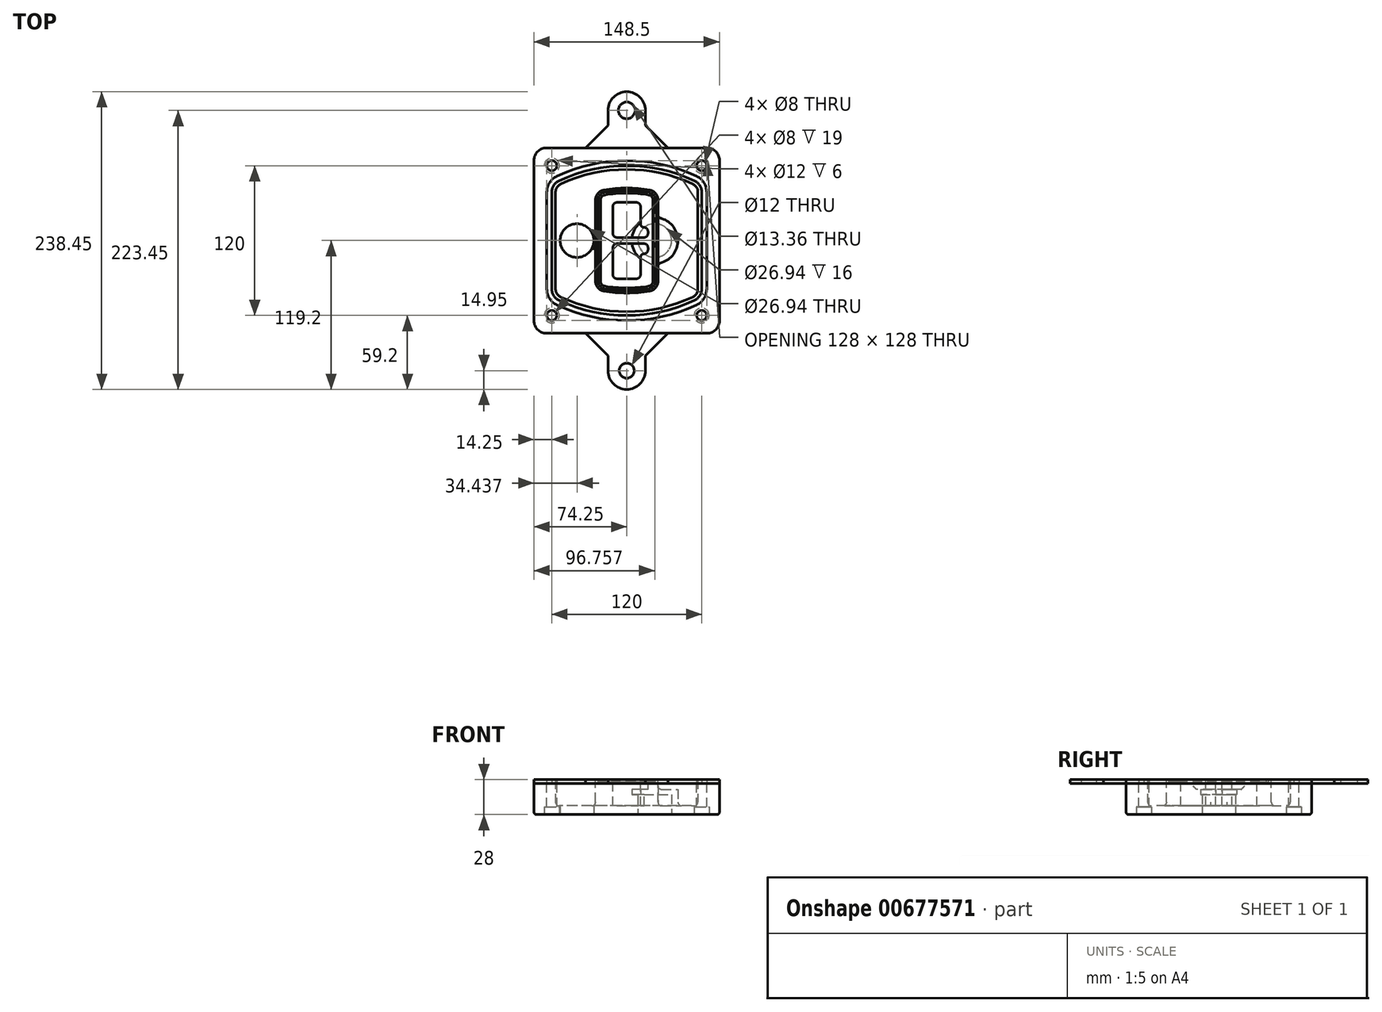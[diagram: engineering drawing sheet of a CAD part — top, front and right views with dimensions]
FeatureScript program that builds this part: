
annotation { "Feature Type Name" : "Feature", "Feature Type Description" : "" }
export const myFeature = defineFeature(function(context is Context, id is Id, definition is map)
    precondition{}
    {
        {
            var Q0;
            Q0=qCreatedBy(makeId("Top.planeOp"),FACE);
            var sketch = newSketch(context, id + "F0", { "sketchPlane" : qUnion([Q0])});
            skPoint(sketch, "E0.rect.middle", {"position": v(0, 0) * mm});
            skLineSegment(sketch, "E1.bottom", {"start": v(-64.25, -74.25) * mm, "end": v(64.25, -74.25) * mm});
            skLineSegment(sketch, "E1.top", {"start": v(-64.25, 74.25) * mm, "end": v(64.25, 74.25) * mm});
            skLineSegment(sketch, "E1.left", {"start": v(-74.25, -64.25) * mm, "end": v(-74.25, 64.25) * mm});
            skLineSegment(sketch, "E1.right", {"start": v(74.25, -64.25) * mm, "end": v(74.25, 64.25) * mm});
            skLineSegment(sketch, "E2", {"start": v(-74.25, 74.25) * mm, "end": v(74.25, -74.25) * mm, "construction": true});
            skLineSegment(sketch, "E3", {"start": v(74.25, 74.25) * mm, "end": v(-74.25, -74.25) * mm, "construction": true});
            skCircle(sketch, "E4", {"center": v(-60, 60) * mm, "radius": 4 * mm});
            skCircle(sketch, "E5", {"center": v(60, 60) * mm, "radius": 4 * mm});
            skCircle(sketch, "E6", {"center": v(60, -60) * mm, "radius": 4 * mm});
            skCircle(sketch, "E7", {"center": v(-60, -60) * mm, "radius": 4 * mm});
            skLineSegment(sketch, "E8", {"start": v(-60, 60) * mm, "end": v(60, 60) * mm, "construction": true});
            skLineSegment(sketch, "E9", {"start": v(60, 60) * mm, "end": v(60, -60) * mm, "construction": true});
            skLineSegment(sketch, "E10", {"start": v(60, -60) * mm, "end": v(-60, -60) * mm, "construction": true});
            skLineSegment(sketch, "E11", {"start": v(-60, -60) * mm, "end": v(-60, 60) * mm, "construction": true});
            skLineSegment(sketch, "E12", {"start": v(-60, 38.83) * mm, "end": v(-60, -38.83) * mm});
            skLineSegment(sketch, "E13", {"start": v(60, 38.83) * mm, "end": v(60, -38.83) * mm});
            skArc(sketch, "E14", {"start": v(54.26, 47.88) * mm, "mid": v(0, 60) * mm, "end": v(-54.26, 47.88) * mm});
            skArc(sketch, "E15", {"start": v(-54.26, -47.88) * mm, "mid": v(0, -60) * mm, "end": v(54.26, -47.88) * mm});
            skLineSegment(sketch, "E16", {"start": v(-60, 0) * mm, "end": v(60, 0) * mm, "construction": true});
            skPoint(sketch, "E17.visualSharp", {"position": v(-60, -45) * mm});
            skArc(sketch, "E17.filletArc", {"start": v(-60, -38.83) * mm, "mid": v(-58.44, -44.2) * mm, "end": v(-54.26, -47.88) * mm});
            skPoint(sketch, "E18.visualSharp", {"position": v(-60, 45) * mm});
            skArc(sketch, "E18.filletArc", {"start": v(-54.26, 47.88) * mm, "mid": v(-58.44, 44.2) * mm, "end": v(-60, 38.83) * mm});
            skPoint(sketch, "E19.visualSharp", {"position": v(60, 45) * mm});
            skArc(sketch, "E19.filletArc", {"start": v(60, 38.83) * mm, "mid": v(58.44, 44.2) * mm, "end": v(54.26, 47.88) * mm});
            skPoint(sketch, "E20.visualSharp", {"position": v(60, -45) * mm});
            skArc(sketch, "E20.filletArc", {"start": v(54.26, -47.88) * mm, "mid": v(58.44, -44.2) * mm, "end": v(60, -38.83) * mm});
            skPoint(sketch, "E21.visualSharp", {"position": v(-74.25, 74.25) * mm});
            skArc(sketch, "E21.filletArc", {"start": v(-64.25, 74.25) * mm, "mid": v(-71.32, 71.32) * mm, "end": v(-74.25, 64.25) * mm});
            skPoint(sketch, "E22.visualSharp", {"position": v(74.25, 74.25) * mm});
            skArc(sketch, "E22.filletArc", {"start": v(74.25, 64.25) * mm, "mid": v(71.32, 71.32) * mm, "end": v(64.25, 74.25) * mm});
            skPoint(sketch, "E23.visualSharp", {"position": v(74.25, -74.25) * mm});
            skArc(sketch, "E23.filletArc", {"start": v(64.25, -74.25) * mm, "mid": v(71.32, -71.32) * mm, "end": v(74.25, -64.25) * mm});
            skPoint(sketch, "E24.visualSharp", {"position": v(-74.25, -74.25) * mm});
            skArc(sketch, "E24.filletArc", {"start": v(-74.25, -64.25) * mm, "mid": v(-71.32, -71.32) * mm, "end": v(-64.25, -74.25) * mm});
            skArc(sketch, "E25.0", {"start": v(57, 38.83) * mm, "mid": v(55.9, 42.58) * mm, "end": v(52.98, 45.17) * mm});
            skLineSegment(sketch, "E25.1", {"start": v(57, 38.83) * mm, "end": v(57, -38.83) * mm});
            skArc(sketch, "E25.2", {"start": v(52.98, -45.17) * mm, "mid": v(55.9, -42.58) * mm, "end": v(57, -38.83) * mm});
            skArc(sketch, "E25.3", {"start": v(-52.98, -45.17) * mm, "mid": v(0, -57) * mm, "end": v(52.98, -45.17) * mm});
            skArc(sketch, "E25.4", {"start": v(-57, -38.83) * mm, "mid": v(-55.9, -42.58) * mm, "end": v(-52.98, -45.17) * mm});
            skArc(sketch, "E25.5", {"start": v(52.98, 45.17) * mm, "mid": v(0, 57) * mm, "end": v(-52.98, 45.17) * mm});
            skLineSegment(sketch, "E25.6", {"start": v(-57, 38.83) * mm, "end": v(-57, -38.83) * mm});
            skArc(sketch, "E25.7", {"start": v(-52.98, 45.17) * mm, "mid": v(-55.9, 42.58) * mm, "end": v(-57, 38.83) * mm});
            skArc(sketch, "E26.0", {"start": v(-55.96, 51.5) * mm, "mid": v(-61.82, 46.33) * mm, "end": v(-64, 38.83) * mm});
            skArc(sketch, "E26.1", {"start": v(55.96, 51.5) * mm, "mid": v(0, 64) * mm, "end": v(-55.96, 51.5) * mm});
            skArc(sketch, "E26.2", {"start": v(64, 38.83) * mm, "mid": v(61.82, 46.33) * mm, "end": v(55.96, 51.5) * mm});
            skLineSegment(sketch, "E26.3", {"start": v(64, 38.83) * mm, "end": v(64, -38.83) * mm});
            skArc(sketch, "E26.4", {"start": v(55.96, -51.5) * mm, "mid": v(61.82, -46.33) * mm, "end": v(64, -38.83) * mm});
            skLineSegment(sketch, "E26.5", {"start": v(-64, 38.83) * mm, "end": v(-64, -38.83) * mm});
            skArc(sketch, "E26.6", {"start": v(-55.96, -51.5) * mm, "mid": v(0, -64) * mm, "end": v(55.96, -51.5) * mm});
            skArc(sketch, "E26.7", {"start": v(-64, -38.83) * mm, "mid": v(-61.82, -46.33) * mm, "end": v(-55.96, -51.5) * mm});
            skSolve(sketch);
        }
        {
            var Q0;
            Q0=makeQuery(id+"F0.imprint","IMPRINT",FACE,{"disambiguationData":[TD([[makeQuery(id+"F0.imprint","IMPRINT",EDGE,{"derivedFrom":sQuery(id+"F0.wireOp",EDGE,"E1.bottom")}),1.0]])]});
            var Q1;
            Q1=makeQuery(id+"F0.imprint","IMPRINT",FACE,{"disambiguationData":[TD([[makeQuery(id+"F0.imprint","IMPRINT",EDGE,{"derivedFrom":sQuery(id+"F0.wireOp",EDGE,"E12")}),1.0]])]});
            var Q2;
            Q2=makeQuery(id+"F0.imprint","IMPRINT",FACE,{"disambiguationData":[TD([[makeQuery(id+"F0.imprint","IMPRINT",EDGE,{"derivedFrom":sQuery(id+"F0.wireOp",EDGE,"E25.0")}),1.0]])]});
            var Q3;
            Q3=makeQuery(id+"F0.imprint","IMPRINT",FACE,{"disambiguationData":[TD([[makeQuery(id+"F0.imprint","IMPRINT",EDGE,{"derivedFrom":sQuery(id+"F0.wireOp",EDGE,"E12")}),-1.0]])]});
            extrude(context, id + "F1", {"entities" : qUnion([Q0, Q1, Q2, Q3]), "oppositeDirection" : true, "depth" : 25 * mm});
        }
        {
            var Q0;
            Q0=makeQuery(id+"F0.imprint","IMPRINT",FACE,{"disambiguationData":[TD([[makeQuery(id+"F0.imprint","IMPRINT",EDGE,{"derivedFrom":sQuery(id+"F0.wireOp",EDGE,"E12")}),1.0]])]});
            extrude(context, id + "F2", {"entities" : qUnion([Q0]), "operationType" : NewBodyOperationType.ADD, "depth" : 3 * mm});
        }
        {
            var Q0;
            Q0=makeQuery(id+"F0.imprint","IMPRINT",FACE,{"disambiguationData":[TD([[makeQuery(id+"F0.imprint","IMPRINT",EDGE,{"derivedFrom":sQuery(id+"F0.wireOp",EDGE,"E25.0")}),1.0]])]});
            extrude(context, id + "F3", {"entities" : qUnion([Q0]), "operationType" : NewBodyOperationType.REMOVE, "oppositeDirection" : true, "depth" : 18 * mm});
        }
        {
            var Q0;
            Q0=makeQuery(id+"F2.opExtrude","CAP_FACE",FACE,{"disambiguationData":[OSD([sQuery(id+"F0.wireOp",EDGE,"E12"),sQuery(id+"F0.wireOp",EDGE,"E13"),sQuery(id+"F0.wireOp",EDGE,"E14"),sQuery(id+"F0.wireOp",EDGE,"E15"),sQuery(id+"F0.wireOp",EDGE,"E17.filletArc"),sQuery(id+"F0.wireOp",EDGE,"E18.filletArc"),sQuery(id+"F0.wireOp",EDGE,"E19.filletArc"),sQuery(id+"F0.wireOp",EDGE,"E20.filletArc"),sQuery(id+"F0.wireOp",EDGE,"E25.0"),sQuery(id+"F0.wireOp",EDGE,"E25.1"),sQuery(id+"F0.wireOp",EDGE,"E25.2"),sQuery(id+"F0.wireOp",EDGE,"E25.3"),sQuery(id+"F0.wireOp",EDGE,"E25.4"),sQuery(id+"F0.wireOp",EDGE,"E25.5"),sQuery(id+"F0.wireOp",EDGE,"E25.6"),sQuery(id+"F0.wireOp",EDGE,"E25.7")])],"isStart":false});
            var sketch = newSketch(context, id + "F4", { "sketchPlane" : qUnion([Q0])});
            skArc(sketch, "E27.0", {"start": v(-18.34, -40.45) * mm, "mid": v(0, -42) * mm, "end": v(18.34, -40.45) * mm});
            skArc(sketch, "E28.0", {"start": v(18.34, 40.45) * mm, "mid": v(0, 42) * mm, "end": v(-18.34, 40.45) * mm});
            skLineSegment(sketch, "E29", {"start": v(-25, 32.57) * mm, "end": v(-25, -32.57) * mm});
            skLineSegment(sketch, "E30", {"start": v(25, 32.57) * mm, "end": v(25, -32.57) * mm});
            skLineSegment(sketch, "E31", {"start": v(-25, 39.1) * mm, "end": v(25, 39.1) * mm, "construction": true});
            skLineSegment(sketch, "E32", {"start": v(-25, -39.1) * mm, "end": v(25, -39.1) * mm, "construction": true});
            skPoint(sketch, "E33.visualSharp", {"position": v(-25, 39.1) * mm});
            skArc(sketch, "E33.filletArc", {"start": v(-18.34, 40.45) * mm, "mid": v(-23.11, 37.73) * mm, "end": v(-25, 32.57) * mm});
            skPoint(sketch, "E34.visualSharp", {"position": v(25, 39.1) * mm});
            skArc(sketch, "E34.filletArc", {"start": v(25, 32.57) * mm, "mid": v(23.11, 37.73) * mm, "end": v(18.34, 40.45) * mm});
            skPoint(sketch, "E35.visualSharp", {"position": v(25, -39.1) * mm});
            skArc(sketch, "E35.filletArc", {"start": v(18.34, -40.45) * mm, "mid": v(23.11, -37.73) * mm, "end": v(25, -32.57) * mm});
            skPoint(sketch, "E36.visualSharp", {"position": v(-25, -39.1) * mm});
            skArc(sketch, "E36.filletArc", {"start": v(-25, -32.57) * mm, "mid": v(-23.11, -37.73) * mm, "end": v(-18.34, -40.45) * mm});
            skArc(sketch, "E37.0", {"start": v(52.98, 45.17) * mm, "mid": v(0, 57) * mm, "end": v(-52.98, 45.17) * mm});
            skArc(sketch, "E37.1", {"start": v(-52.98, 45.17) * mm, "mid": v(-55.9, 42.58) * mm, "end": v(-57, 38.83) * mm});
            skLineSegment(sketch, "E37.2", {"start": v(-57, 38.83) * mm, "end": v(-57, -38.83) * mm});
            skArc(sketch, "E37.3", {"start": v(-57, -38.83) * mm, "mid": v(-55.9, -42.58) * mm, "end": v(-52.98, -45.17) * mm});
            skArc(sketch, "E37.4", {"start": v(-52.98, -45.17) * mm, "mid": v(0, -57) * mm, "end": v(52.98, -45.17) * mm});
            skArc(sketch, "E37.5", {"start": v(52.98, -45.17) * mm, "mid": v(55.9, -42.58) * mm, "end": v(57, -38.83) * mm});
            skLineSegment(sketch, "E37.6", {"start": v(57, 38.83) * mm, "end": v(57, -38.83) * mm});
            skArc(sketch, "E37.7", {"start": v(57, 38.83) * mm, "mid": v(55.9, 42.58) * mm, "end": v(52.98, 45.17) * mm});
            skLineSegment(sketch, "E38.0", {"start": v(23, 32.57) * mm, "end": v(23, -32.57) * mm});
            skArc(sketch, "E38.1", {"start": v(18, -38.48) * mm, "mid": v(21.58, -36.44) * mm, "end": v(23, -32.57) * mm});
            skArc(sketch, "E38.2", {"start": v(-18, -38.48) * mm, "mid": v(0, -40) * mm, "end": v(18, -38.48) * mm});
            skArc(sketch, "E38.3", {"start": v(-23, -32.57) * mm, "mid": v(-21.58, -36.44) * mm, "end": v(-18, -38.48) * mm});
            skLineSegment(sketch, "E38.4", {"start": v(-23, 32.57) * mm, "end": v(-23, -32.57) * mm});
            skArc(sketch, "E38.5", {"start": v(23, 32.57) * mm, "mid": v(21.58, 36.44) * mm, "end": v(18, 38.48) * mm});
            skArc(sketch, "E38.6", {"start": v(-18, 38.48) * mm, "mid": v(-21.58, 36.44) * mm, "end": v(-23, 32.57) * mm});
            skArc(sketch, "E38.7", {"start": v(18, 38.48) * mm, "mid": v(0, 40) * mm, "end": v(-18, 38.48) * mm});
            skArc(sketch, "E39.0", {"start": v(21, 32.57) * mm, "mid": v(20.06, 35.15) * mm, "end": v(17.67, 36.5) * mm});
            skLineSegment(sketch, "E39.1", {"start": v(21, 32.57) * mm, "end": v(21, -32.57) * mm});
            skArc(sketch, "E39.2", {"start": v(17.67, -36.5) * mm, "mid": v(20.06, -35.15) * mm, "end": v(21, -32.57) * mm});
            skArc(sketch, "E39.3", {"start": v(-17.67, -36.5) * mm, "mid": v(0, -38) * mm, "end": v(17.67, -36.5) * mm});
            skArc(sketch, "E39.4", {"start": v(-21, -32.57) * mm, "mid": v(-20.06, -35.15) * mm, "end": v(-17.67, -36.5) * mm});
            skArc(sketch, "E39.5", {"start": v(17.67, 36.5) * mm, "mid": v(0, 38) * mm, "end": v(-17.67, 36.5) * mm});
            skLineSegment(sketch, "E39.6", {"start": v(-21, 32.57) * mm, "end": v(-21, -32.57) * mm});
            skArc(sketch, "E39.7", {"start": v(-17.67, 36.5) * mm, "mid": v(-20.06, 35.15) * mm, "end": v(-21, 32.57) * mm});
            skLineSegment(sketch, "E40", {"start": v(-25, 0) * mm, "end": v(25, 0) * mm, "construction": true});
            skLineSegment(sketch, "E41", {"start": v(-11, 5.5) * mm, "end": v(-11, 27.5) * mm});
            skLineSegment(sketch, "E42", {"start": v(-8, 30.5) * mm, "end": v(8, 30.5) * mm});
            skLineSegment(sketch, "E43", {"start": v(11, 27.5) * mm, "end": v(11, 13.5) * mm});
            skLineSegment(sketch, "E44", {"start": v(14, 10.5) * mm, "end": v(14, 10.5) * mm});
            skLineSegment(sketch, "E45", {"start": v(17, 7.5) * mm, "end": v(17, 5.5) * mm});
            skLineSegment(sketch, "E46", {"start": v(14, 2.5) * mm, "end": v(-8, 2.5) * mm});
            skPoint(sketch, "E47.visualSharp", {"position": v(-11, 30.5) * mm});
            skArc(sketch, "E47.filletArc", {"start": v(-8, 30.5) * mm, "mid": v(-10.12, 29.62) * mm, "end": v(-11, 27.5) * mm});
            skPoint(sketch, "E48.visualSharp", {"position": v(11, 30.5) * mm});
            skArc(sketch, "E48.filletArc", {"start": v(11, 27.5) * mm, "mid": v(10.12, 29.62) * mm, "end": v(8, 30.5) * mm});
            skPoint(sketch, "E49.visualSharp", {"position": v(11, 10.5) * mm});
            skArc(sketch, "E49.filletArc", {"start": v(11, 13.5) * mm, "mid": v(11.88, 11.38) * mm, "end": v(14, 10.5) * mm});
            skPoint(sketch, "E50.visualSharp", {"position": v(17, 10.5) * mm});
            skArc(sketch, "E50.filletArc", {"start": v(17, 7.5) * mm, "mid": v(16.12, 9.62) * mm, "end": v(14, 10.5) * mm});
            skPoint(sketch, "E51.visualSharp", {"position": v(17, 2.5) * mm});
            skArc(sketch, "E51.filletArc", {"start": v(14, 2.5) * mm, "mid": v(16.12, 3.38) * mm, "end": v(17, 5.5) * mm});
            skPoint(sketch, "E52.visualSharp", {"position": v(-11, 2.5) * mm});
            skArc(sketch, "E52.filletArc", {"start": v(-11, 5.5) * mm, "mid": v(-10.12, 3.38) * mm, "end": v(-8, 2.5) * mm});
            skLineSegment(sketch, "E53.0.MirrorCS", {"start": v(14, -2.5) * mm, "end": v(-8, -2.5) * mm});
            skArc(sketch, "E54.0.MirrorCS", {"start": v(-11, -5.5) * mm, "mid": v(-10.12, -3.38) * mm, "end": v(-8, -2.5) * mm});
            skLineSegment(sketch, "E55.0.MirrorCS", {"start": v(-11, -5.5) * mm, "end": v(-11, -27.5) * mm});
            skArc(sketch, "E56.0.MirrorCS", {"start": v(-8, -30.5) * mm, "mid": v(-10.12, -29.62) * mm, "end": v(-11, -27.5) * mm});
            skLineSegment(sketch, "E57.0.MirrorCS", {"start": v(-8, -30.5) * mm, "end": v(8, -30.5) * mm});
            skArc(sketch, "E58.0.MirrorCS", {"start": v(11, -27.5) * mm, "mid": v(10.12, -29.62) * mm, "end": v(8, -30.5) * mm});
            skLineSegment(sketch, "E59.0.MirrorCS", {"start": v(11, -27.5) * mm, "end": v(11, -13.5) * mm});
            skArc(sketch, "E60.0.MirrorCS", {"start": v(11, -13.5) * mm, "mid": v(11.88, -11.38) * mm, "end": v(14, -10.5) * mm});
            skArc(sketch, "E61.0.MirrorCS", {"start": v(17, -7.5) * mm, "mid": v(16.12, -9.62) * mm, "end": v(14, -10.5) * mm});
            skLineSegment(sketch, "E62.0.MirrorCS", {"start": v(17, -7.5) * mm, "end": v(17, -5.5) * mm});
            skArc(sketch, "E63.0.MirrorCS", {"start": v(14, -2.5) * mm, "mid": v(16.12, -3.38) * mm, "end": v(17, -5.5) * mm});
            skSolve(sketch);
        }
        {
            var Q0;
            Q0=makeQuery(id+"F4.imprint","IMPRINT",FACE,{"disambiguationData":[TD([[makeQuery(id+"F4.imprint","IMPRINT",EDGE,{"derivedFrom":sQuery(id+"F4.wireOp",EDGE,"E27.0")}),1.0]])]});
            var Q1;
            Q1=makeQuery(id+"F4.imprint","IMPRINT",FACE,{"disambiguationData":[TD([[makeQuery(id+"F4.imprint","IMPRINT",EDGE,{"derivedFrom":sQuery(id+"F4.wireOp",EDGE,"E38.0")}),-1.0]])]});
            var Q2;
            Q2=makeQuery(id+"F4.imprint","IMPRINT",FACE,{"disambiguationData":[TD([[makeQuery(id+"F4.imprint","IMPRINT",EDGE,{"derivedFrom":sQuery(id+"F4.wireOp",EDGE,"E39.0")}),1.0]])]});
            extrude(context, id + "F5", {"entities" : qUnion([Q0, Q1, Q2]), "operationType" : NewBodyOperationType.ADD, "endBound" : BoundingType.UP_TO_NEXT, "oppositeDirection" : true, "depth" : 25 * mm});
        }
        {
            var Q0;
            Q0=makeQuery(id+"F4.imprint","IMPRINT",FACE,{"disambiguationData":[TD([[makeQuery(id+"F4.imprint","IMPRINT",EDGE,{"derivedFrom":sQuery(id+"F4.wireOp",EDGE,"E38.0")}),-1.0]])]});
            extrude(context, id + "F6", {"entities" : qUnion([Q0]), "operationType" : NewBodyOperationType.REMOVE, "oppositeDirection" : true, "depth" : 2 * mm});
        }
        {
            var Q0;
            Q0=makeQuery(id+"F1.opExtrude","CAP_FACE",FACE,{"disambiguationData":[OSD([sQuery(id+"F0.wireOp",EDGE,"E1.bottom"),sQuery(id+"F0.wireOp",EDGE,"E1.top"),sQuery(id+"F0.wireOp",EDGE,"E1.left"),sQuery(id+"F0.wireOp",EDGE,"E1.right"),sQuery(id+"F0.wireOp",EDGE,"E4"),sQuery(id+"F0.wireOp",EDGE,"E5"),sQuery(id+"F0.wireOp",EDGE,"E6"),sQuery(id+"F0.wireOp",EDGE,"E7"),sQuery(id+"F0.wireOp",EDGE,"E21.filletArc"),sQuery(id+"F0.wireOp",EDGE,"E22.filletArc"),sQuery(id+"F0.wireOp",EDGE,"E23.filletArc"),sQuery(id+"F0.wireOp",EDGE,"E24.filletArc")])],"isStart":false});
            var sketch = newSketch(context, id + "F7", { "sketchPlane" : qUnion([Q0])});
            skCircle(sketch, "E64", {"center": v(22.5, 0) * mm, "radius": 13.47 * mm});
            skCircle(sketch, "E65", {"center": v(-39.81, 0) * mm, "radius": 13.47 * mm});
            skLineSegment(sketch, "E66", {"start": v(74.25, 0) * mm, "end": v(-74.25, 0) * mm});
            skCircle(sketch, "E67", {"center": v(22.5, 0) * mm, "radius": 18.47 * mm});
            skCircle(sketch, "E68", {"center": v(60, -60) * mm, "radius": 6 * mm});
            skCircle(sketch, "E69", {"center": v(-60, -60) * mm, "radius": 6 * mm});
            skCircle(sketch, "E70", {"center": v(-60, 60) * mm, "radius": 6 * mm});
            skCircle(sketch, "E71", {"center": v(60, 60) * mm, "radius": 6 * mm});
            skSolve(sketch);
        }
        {
            var Q0;
            {var subQ1=sQuery(id+"F7.wireOp",EDGE,"E66");var subQ4=sQuery(id+"F7.wireOp",EDGE,"E64");var subQ6=makeQuery(id+"F7.imprint","INTERSECT",VERTEX,{"disambiguationData":[OD(0.0)],"derivedFrom":[subQ4,subQ1]});Q0=makeQuery(id+"F7.imprint","IMPRINT",FACE,{"disambiguationData":[TD([[makeQuery(id+"F7.imprint","IMPRINT",EDGE,{"disambiguationData":[TD([[subQ6,-1.0]])],"derivedFrom":subQ4}),-1.0]])]});}
            var Q1;
            {var subQ0=sQuery(id+"F7.wireOp",EDGE,"E66");var subQ1=sQuery(id+"F7.wireOp",EDGE,"E64");var subQ3=makeQuery(id+"F7.imprint","INTERSECT",VERTEX,{"disambiguationData":[OD(0.0)],"derivedFrom":[subQ1,subQ0]});Q1=makeQuery(id+"F7.imprint","IMPRINT",FACE,{"disambiguationData":[TD([[makeQuery(id+"F7.imprint","IMPRINT",EDGE,{"disambiguationData":[TD([[subQ3,-1.0]])],"derivedFrom":subQ1}),1.0]])]});}
            var Q2;
            {var subQ0=sQuery(id+"F7.wireOp",EDGE,"E66");var subQ1=sQuery(id+"F7.wireOp",EDGE,"E64");var subQ3=makeQuery(id+"F7.imprint","INTERSECT",VERTEX,{"disambiguationData":[OD(0.0)],"derivedFrom":[subQ1,subQ0]});Q2=makeQuery(id+"F7.imprint","IMPRINT",FACE,{"disambiguationData":[TD([[makeQuery(id+"F7.imprint","IMPRINT",EDGE,{"disambiguationData":[TD([[subQ3,1.0]])],"derivedFrom":subQ1}),1.0]])]});}
            var Q3;
            {var subQ1=sQuery(id+"F7.wireOp",EDGE,"E66");var subQ4=sQuery(id+"F7.wireOp",EDGE,"E64");var subQ6=makeQuery(id+"F7.imprint","INTERSECT",VERTEX,{"disambiguationData":[OD(0.0)],"derivedFrom":[subQ4,subQ1]});Q3=makeQuery(id+"F7.imprint","IMPRINT",FACE,{"disambiguationData":[TD([[makeQuery(id+"F7.imprint","IMPRINT",EDGE,{"disambiguationData":[TD([[subQ6,1.0]])],"derivedFrom":subQ4}),-1.0]])]});}
            extrude(context, id + "F8", {"entities" : qUnion([Q0, Q1, Q2, Q3]), "operationType" : NewBodyOperationType.ADD, "oppositeDirection" : true, "depth" : 20 * mm});
        }
        {
            var Q0;
            {var subQ0=sQuery(id+"F7.wireOp",EDGE,"E66");var subQ1=sQuery(id+"F7.wireOp",EDGE,"E64");var subQ3=makeQuery(id+"F7.imprint","INTERSECT",VERTEX,{"disambiguationData":[OD(0.0)],"derivedFrom":[subQ1,subQ0]});Q0=makeQuery(id+"F7.imprint","IMPRINT",FACE,{"disambiguationData":[TD([[makeQuery(id+"F7.imprint","IMPRINT",EDGE,{"disambiguationData":[TD([[subQ3,-1.0]])],"derivedFrom":subQ1}),1.0]])]});}
            var Q1;
            {var subQ0=sQuery(id+"F7.wireOp",EDGE,"E66");var subQ1=sQuery(id+"F7.wireOp",EDGE,"E64");var subQ3=makeQuery(id+"F7.imprint","INTERSECT",VERTEX,{"disambiguationData":[OD(0.0)],"derivedFrom":[subQ1,subQ0]});Q1=makeQuery(id+"F7.imprint","IMPRINT",FACE,{"disambiguationData":[TD([[makeQuery(id+"F7.imprint","IMPRINT",EDGE,{"disambiguationData":[TD([[subQ3,1.0]])],"derivedFrom":subQ1}),1.0]])]});}
            extrude(context, id + "F9", {"entities" : qUnion([Q0, Q1]), "operationType" : NewBodyOperationType.REMOVE, "oppositeDirection" : true, "depth" : 16 * mm});
        }
        {
            var Q0;
            {var subQ0=sQuery(id+"F7.wireOp",EDGE,"E66");var subQ1=sQuery(id+"F7.wireOp",EDGE,"E65");var subQ3=makeQuery(id+"F7.imprint","INTERSECT",VERTEX,{"disambiguationData":[OD(0.0)],"derivedFrom":[subQ1,subQ0]});Q0=makeQuery(id+"F7.imprint","IMPRINT",FACE,{"disambiguationData":[TD([[makeQuery(id+"F7.imprint","IMPRINT",EDGE,{"disambiguationData":[TD([[subQ3,-1.0]])],"derivedFrom":subQ1}),1.0]])]});}
            var Q1;
            {var subQ0=sQuery(id+"F7.wireOp",EDGE,"E66");var subQ1=sQuery(id+"F7.wireOp",EDGE,"E65");var subQ3=makeQuery(id+"F7.imprint","INTERSECT",VERTEX,{"disambiguationData":[OD(0.0)],"derivedFrom":[subQ1,subQ0]});Q1=makeQuery(id+"F7.imprint","IMPRINT",FACE,{"disambiguationData":[TD([[makeQuery(id+"F7.imprint","IMPRINT",EDGE,{"disambiguationData":[TD([[subQ3,1.0]])],"derivedFrom":subQ1}),1.0]])]});}
            extrude(context, id + "F10", {"entities" : qUnion([Q0, Q1]), "operationType" : NewBodyOperationType.REMOVE, "oppositeDirection" : true, "depth" : 25 * mm});
        }
        {
            var Q0;
            Q0=makeQuery(id+"F7.imprint","IMPRINT",FACE,{"disambiguationData":[TD([[makeQuery(id+"F7.imprint","IMPRINT",EDGE,{"derivedFrom":sQuery(id+"F7.wireOp",EDGE,"E68")}),1.0]])]});
            var Q1;
            Q1=makeQuery(id+"F7.imprint","IMPRINT",FACE,{"disambiguationData":[TD([[makeQuery(id+"F7.imprint","IMPRINT",EDGE,{"derivedFrom":makeQuery(id+"F1.opExtrude","CAP_EDGE",EDGE,{"disambiguationData":[OSD([sQuery(id+"F0.wireOp",EDGE,"E5")])],"isStart":false})}),-1.0]])]});
            var Q2;
            Q2=makeQuery(id+"F7.imprint","IMPRINT",FACE,{"disambiguationData":[TD([[makeQuery(id+"F7.imprint","IMPRINT",EDGE,{"derivedFrom":sQuery(id+"F7.wireOp",EDGE,"E69")}),1.0]])]});
            var Q3;
            Q3=makeQuery(id+"F7.imprint","IMPRINT",FACE,{"disambiguationData":[TD([[makeQuery(id+"F7.imprint","IMPRINT",EDGE,{"derivedFrom":makeQuery(id+"F1.opExtrude","CAP_EDGE",EDGE,{"disambiguationData":[OSD([sQuery(id+"F0.wireOp",EDGE,"E4")])],"isStart":false})}),-1.0]])]});
            var Q4;
            Q4=makeQuery(id+"F7.imprint","IMPRINT",FACE,{"disambiguationData":[TD([[makeQuery(id+"F7.imprint","IMPRINT",EDGE,{"derivedFrom":sQuery(id+"F7.wireOp",EDGE,"E70")}),1.0]])]});
            var Q5;
            Q5=makeQuery(id+"F7.imprint","IMPRINT",FACE,{"disambiguationData":[TD([[makeQuery(id+"F7.imprint","IMPRINT",EDGE,{"derivedFrom":makeQuery(id+"F1.opExtrude","CAP_EDGE",EDGE,{"disambiguationData":[OSD([sQuery(id+"F0.wireOp",EDGE,"E7")])],"isStart":false})}),-1.0]])]});
            var Q6;
            Q6=makeQuery(id+"F7.imprint","IMPRINT",FACE,{"disambiguationData":[TD([[makeQuery(id+"F7.imprint","IMPRINT",EDGE,{"derivedFrom":sQuery(id+"F7.wireOp",EDGE,"E71")}),1.0]])]});
            var Q7;
            Q7=makeQuery(id+"F7.imprint","IMPRINT",FACE,{"disambiguationData":[TD([[makeQuery(id+"F7.imprint","IMPRINT",EDGE,{"derivedFrom":makeQuery(id+"F1.opExtrude","CAP_EDGE",EDGE,{"disambiguationData":[OSD([sQuery(id+"F0.wireOp",EDGE,"E6")])],"isStart":false})}),-1.0]])]});
            extrude(context, id + "F11", {"entities" : qUnion([Q0, Q1, Q2, Q3, Q4, Q5, Q6, Q7]), "operationType" : NewBodyOperationType.REMOVE, "oppositeDirection" : true, "depth" : 6 * mm});
        }
        {
            var Q0;
            Q0=makeQuery(id+"F9.boolean.opBoolean","COPY",FACE,{"derivedFrom":makeQuery(id+"F9.opExtrude","CAP_FACE",FACE,{"disambiguationData":[OSD([sQuery(id+"F7.wireOp",EDGE,"E64")])],"isStart":false})});
            var sketch = newSketch(context, id + "F12", { "sketchPlane" : qUnion([Q0])});
            skArc(sketch, "E72.0", {"start": v(11, 14.45) * mm, "mid": v(6.45, 9.13) * mm, "end": v(4.2, 2.5) * mm});
            skArc(sketch, "E72.1", {"start": v(4.2, -2.5) * mm, "mid": v(6.45, -9.13) * mm, "end": v(11, -14.45) * mm});
            skLineSegment(sketch, "E73", {"start": v(4.2, -2.5) * mm, "end": v(14, -2.5) * mm});
            skLineSegment(sketch, "E74.0", {"start": v(14, 2.5) * mm, "end": v(4.2, 2.5) * mm});
            skArc(sketch, "E74.1", {"start": v(14, 2.5) * mm, "mid": v(16.12, 3.38) * mm, "end": v(17, 5.5) * mm});
            skLineSegment(sketch, "E74.2", {"start": v(17, 7.5) * mm, "end": v(17, 5.5) * mm});
            skArc(sketch, "E74.3", {"start": v(17, 7.5) * mm, "mid": v(16.12, 9.62) * mm, "end": v(14, 10.5) * mm});
            skArc(sketch, "E74.4", {"start": v(11, 13.5) * mm, "mid": v(11.88, 11.38) * mm, "end": v(14, 10.5) * mm});
            skLineSegment(sketch, "E74.5", {"start": v(11, 14.45) * mm, "end": v(11, 13.5) * mm});
            skLineSegment(sketch, "E74.7", {"start": v(14, -2.5) * mm, "end": v(4.2, -2.5) * mm});
            skArc(sketch, "E74.8", {"start": v(14, -2.5) * mm, "mid": v(16.12, -3.38) * mm, "end": v(17, -5.5) * mm});
            skLineSegment(sketch, "E74.9", {"start": v(17, -7.5) * mm, "end": v(17, -5.5) * mm});
            skArc(sketch, "E74.10", {"start": v(17, -7.5) * mm, "mid": v(16.12, -9.62) * mm, "end": v(14, -10.5) * mm});
            skArc(sketch, "E74.11", {"start": v(11, -13.5) * mm, "mid": v(11.88, -11.38) * mm, "end": v(14, -10.5) * mm});
            skLineSegment(sketch, "E74.12", {"start": v(11, -14.45) * mm, "end": v(11, -13.5) * mm});
            skPoint(sketch, "E75.orphan", {"position": v(11, -27.5) * mm});
            skPoint(sketch, "E76.orphan", {"position": v(-8, -2.5) * mm});
            skPoint(sketch, "E77.orphan", {"position": v(-8, 2.5) * mm});
            skPoint(sketch, "E78.orphan", {"position": v(11, 27.5) * mm});
            skSolve(sketch);
        }
        {
            var Q0;
            {var subQ7=sQuery(id+"F12.wireOp",EDGE,"E72.0");var subQ14=sQuery(id+"F12.wireOp",EDGE,"E72.1");var subQ16=sQuery(id+"F12.wireOp",EDGE,"E74.1");var subQ18=sQuery(id+"F12.wireOp",EDGE,"E74.8");Q0=qUnion([makeQuery(id+"F12.imprint","IMPRINT",FACE,{"disambiguationData":[TD([[makeQuery(id+"F12.imprint","IMPRINT",EDGE,{"derivedFrom":subQ7}),1.0]])]}),makeQuery(id+"F12.imprint","IMPRINT",FACE,{"disambiguationData":[TD([[makeQuery(id+"F12.imprint","IMPRINT",EDGE,{"derivedFrom":subQ14}),1.0]])]}),makeQuery(id+"F12.imprint","IMPRINT",FACE,{"disambiguationData":[TD([[makeQuery(id+"F12.imprint","IMPRINT",EDGE,{"derivedFrom":subQ16}),1.0]])]}),makeQuery(id+"F12.imprint","IMPRINT",FACE,{"disambiguationData":[TD([[makeQuery(id+"F12.imprint","IMPRINT",EDGE,{"derivedFrom":subQ18}),-1.0]])]})]);}
            var Q1;
            Q1=makeQuery(id+"F5.boolean.opBoolean","SPLIT",FACE,{"disambiguationData":[TD([makeQuery(id+"F5.opExtrude","SWEPT_FACE",FACE,{"disambiguationData":[OSD([sQuery(id+"F4.wireOp",EDGE,"E41")])]})])],"derivedFrom":makeQuery(id+"F3.boolean.opBoolean","COPY",FACE,{"derivedFrom":makeQuery(id+"F3.opExtrude","CAP_FACE",FACE,{"disambiguationData":[OSD([sQuery(id+"F0.wireOp",EDGE,"E25.0"),sQuery(id+"F0.wireOp",EDGE,"E25.1"),sQuery(id+"F0.wireOp",EDGE,"E25.2"),sQuery(id+"F0.wireOp",EDGE,"E25.3"),sQuery(id+"F0.wireOp",EDGE,"E25.4"),sQuery(id+"F0.wireOp",EDGE,"E25.5"),sQuery(id+"F0.wireOp",EDGE,"E25.6"),sQuery(id+"F0.wireOp",EDGE,"E25.7")])],"isStart":false})})});
            extrude(context, id + "F13", {"entities" : qUnion([Q0]), "operationType" : NewBodyOperationType.REMOVE, "endBound" : BoundingType.UP_TO_SURFACE, "endBoundEntityFace" : qUnion([Q1]), "depth" : 25 * mm});
        }
        {
            var Q0;
            Q0=makeQuery(id+"F3.boolean.opBoolean","COPY",EDGE,{"derivedFrom":makeQuery(id+"F3.opExtrude","CAP_EDGE",EDGE,{"disambiguationData":[OSD([sQuery(id+"F0.wireOp",EDGE,"E25.6")])],"isStart":false})});
            var Q1;
            Q1=makeQuery(id+"F8.boolean.opBoolean","INTERSECT",EDGE,{"derivedFrom":[makeQuery(id+"F5.opExtrude","SWEPT_FACE",FACE,{"disambiguationData":[OSD([sQuery(id+"F4.wireOp",EDGE,"E30")])]}),makeQuery(id+"F8.opExtrude","CAP_FACE",FACE,{"disambiguationData":[OSD([sQuery(id+"F7.wireOp",EDGE,"E67")])],"isStart":false})]});
            var Q2;
            Q2=makeQuery(id+"F8.boolean.opBoolean","INTERSECT",EDGE,{"disambiguationData":[OD(1.0)],"derivedFrom":[makeQuery(id+"F5.opExtrude","SWEPT_FACE",FACE,{"disambiguationData":[OSD([sQuery(id+"F4.wireOp",EDGE,"E30")])]}),makeQuery(id+"F8.opExtrude","SWEPT_FACE",FACE,{"disambiguationData":[OSD([sQuery(id+"F7.wireOp",EDGE,"E67")])]})]});
            var Q3;
            {var subQ0=sQuery(id+"F4.wireOp",EDGE,"E30");Q3=makeQuery(id+"F8.boolean.opBoolean","SPLIT",EDGE,{"disambiguationData":[TD([makeQuery(id+"F5.opExtrude","SWEPT_FACE",FACE,{"disambiguationData":[OSD([sQuery(id+"F4.wireOp",EDGE,"E35.filletArc")])]})])],"derivedFrom":makeQuery(id+"F5.opExtrude","CAP_EDGE",EDGE,{"disambiguationData":[OSD([subQ0])],"isStart":false})});}
            var Q4;
            {var subQ0=sQuery(id+"F0.wireOp",EDGE,"E25.7");var subQ1=sQuery(id+"F0.wireOp",EDGE,"E25.1");var subQ2=sQuery(id+"F0.wireOp",EDGE,"E25.6");var subQ3=sQuery(id+"F0.wireOp",EDGE,"E25.5");var subQ4=sQuery(id+"F0.wireOp",EDGE,"E25.4");var subQ5=sQuery(id+"F0.wireOp",EDGE,"E25.0");var subQ6=sQuery(id+"F0.wireOp",EDGE,"E25.2");var subQ7=sQuery(id+"F0.wireOp",EDGE,"E25.3");Q4=makeQuery(id+"F8.boolean.opBoolean","INTERSECT",EDGE,{"derivedFrom":[makeQuery(id+"F5.boolean.opBoolean","SPLIT",FACE,{"disambiguationData":[TD([makeQuery(id+"F2.opExtrude","SWEPT_FACE",FACE,{"disambiguationData":[OSD([subQ5])]})])],"derivedFrom":makeQuery(id+"F3.boolean.opBoolean","COPY",FACE,{"derivedFrom":makeQuery(id+"F3.opExtrude","CAP_FACE",FACE,{"disambiguationData":[OSD([subQ5,subQ1,subQ6,subQ7,subQ4,subQ3,subQ2,subQ0])],"isStart":false})})}),makeQuery(id+"F8.opExtrude","SWEPT_FACE",FACE,{"disambiguationData":[OSD([sQuery(id+"F7.wireOp",EDGE,"E67")])]})]});}
            var Q5;
            Q5=makeQuery(id+"F8.boolean.opBoolean","INTERSECT",EDGE,{"disambiguationData":[OD(0.0)],"derivedFrom":[makeQuery(id+"F5.opExtrude","SWEPT_FACE",FACE,{"disambiguationData":[OSD([sQuery(id+"F4.wireOp",EDGE,"E30")])]}),makeQuery(id+"F8.opExtrude","SWEPT_FACE",FACE,{"disambiguationData":[OSD([sQuery(id+"F7.wireOp",EDGE,"E67")])]})]});
            fillet(context, id + "F14", {"entities" : qUnion([Q0, Q1, Q2, Q3, Q4, Q5]), "radius" : 3 * mm, "tangentPropagation" : true, "allowEdgeOverflow" : false});
        }
        {
            var Q0;
            Q0=makeQuery(id+"F1.opExtrude","CAP_EDGE",EDGE,{"disambiguationData":[OSD([sQuery(id+"F0.wireOp",EDGE,"E1.bottom")])],"isStart":false});
            fillet(context, id + "F15", {"entities" : qUnion([Q0]), "radius" : 2 * mm, "tangentPropagation" : true, "allowEdgeOverflow" : false});
        }
        {
            var Q0;
            {var subQ0=sQuery(id+"F0.wireOp",EDGE,"E21.filletArc");var subQ1=sQuery(id+"F0.wireOp",EDGE,"E7");var subQ2=sQuery(id+"F0.wireOp",EDGE,"E6");var subQ3=sQuery(id+"F0.wireOp",EDGE,"E5");var subQ4=sQuery(id+"F0.wireOp",EDGE,"E4");var subQ5=sQuery(id+"F0.wireOp",EDGE,"E22.filletArc");var subQ6=sQuery(id+"F0.wireOp",EDGE,"E1.bottom");var subQ7=sQuery(id+"F0.wireOp",EDGE,"E1.right");var subQ8=sQuery(id+"F0.wireOp",EDGE,"E1.top");var subQ9=sQuery(id+"F0.wireOp",EDGE,"E1.left");var subQ10=sQuery(id+"F0.wireOp",EDGE,"E23.filletArc");var subQ11=sQuery(id+"F0.wireOp",EDGE,"E24.filletArc");Q0=makeQuery(id+"F2.boolean.opBoolean","SPLIT",FACE,{"disambiguationData":[TD([makeQuery(id+"F1.opExtrude","SWEPT_FACE",FACE,{"disambiguationData":[OSD([subQ6])]})])],"derivedFrom":makeQuery(id+"F1.opExtrude","CAP_FACE",FACE,{"disambiguationData":[OSD([subQ6,subQ8,subQ9,subQ7,subQ4,subQ3,subQ2,subQ1,subQ0,subQ5,subQ10,subQ11])],"isStart":true})});}
            var sketch = newSketch(context, id + "F16", { "sketchPlane" : qUnion([Q0])});
            skCircle(sketch, "E79", {"center": v(0, 104.25) * mm, "radius": 6.68 * mm});
            skLineSegment(sketch, "E80", {"start": v(-15, 92.25) * mm, "end": v(-15, 104.25) * mm});
            skLineSegment(sketch, "E81", {"start": v(-15, 104.25) * mm, "end": v(-15, 92.25) * mm});
            skLineSegment(sketch, "E82", {"start": v(-33, 74.25) * mm, "end": v(-15, 92.25) * mm});
            skArc(sketch, "E83", {"start": v(15, 104.25) * mm, "mid": v(0, 119.25) * mm, "end": v(-15, 104.25) * mm});
            skLineSegment(sketch, "E84", {"start": v(15, 92.25) * mm, "end": v(33, 74.25) * mm});
            skLineSegment(sketch, "E85", {"start": v(15, 104.25) * mm, "end": v(15, 92.25) * mm});
            skCircle(sketch, "E86", {"center": v(0, -104.25) * mm, "radius": 6 * mm});
            skArc(sketch, "E87", {"start": v(-15, -104.25) * mm, "mid": v(0, -119.2) * mm, "end": v(15, -104.25) * mm});
            skLineSegment(sketch, "E88", {"start": v(15, -92.25) * mm, "end": v(15, -104.25) * mm});
            skLineSegment(sketch, "E89", {"start": v(15, -92.25) * mm, "end": v(33, -74.25) * mm});
            skLineSegment(sketch, "E90", {"start": v(-15, -92.25) * mm, "end": v(-15, -104.25) * mm});
            skLineSegment(sketch, "E91", {"start": v(-15, -92.25) * mm, "end": v(-33, -74.25) * mm});
            skSolve(sketch);
        }
        {
            var Q0;
            Q0 = qSketchRegion(id + "F16", true);
            var Q1;
            Q1=makeQuery(id+"F2.opExtrude","CAP_FACE",FACE,{"disambiguationData":[OSD([sQuery(id+"F0.wireOp",EDGE,"E12"),sQuery(id+"F0.wireOp",EDGE,"E13"),sQuery(id+"F0.wireOp",EDGE,"E14"),sQuery(id+"F0.wireOp",EDGE,"E15"),sQuery(id+"F0.wireOp",EDGE,"E17.filletArc"),sQuery(id+"F0.wireOp",EDGE,"E18.filletArc"),sQuery(id+"F0.wireOp",EDGE,"E19.filletArc"),sQuery(id+"F0.wireOp",EDGE,"E20.filletArc"),sQuery(id+"F0.wireOp",EDGE,"E25.0"),sQuery(id+"F0.wireOp",EDGE,"E25.1"),sQuery(id+"F0.wireOp",EDGE,"E25.2"),sQuery(id+"F0.wireOp",EDGE,"E25.3"),sQuery(id+"F0.wireOp",EDGE,"E25.4"),sQuery(id+"F0.wireOp",EDGE,"E25.5"),sQuery(id+"F0.wireOp",EDGE,"E25.6"),sQuery(id+"F0.wireOp",EDGE,"E25.7")])],"isStart":false});
            extrude(context, id + "F17", {"entities" : qUnion([Q0]), "operationType" : NewBodyOperationType.ADD, "endBound" : BoundingType.UP_TO_SURFACE, "depth" : 25 * mm, "endBoundEntityFace" : qUnion([Q1]), "offsetDistance" : 25 * mm});
        }
        {
            var Q0;
            Q0=makeQuery(id+"F16.imprint","IMPRINT",FACE,{"disambiguationData":[TD([[makeQuery(id+"F16.imprint","IMPRINT",EDGE,{"derivedFrom":sQuery(id+"F16.wireOp",EDGE,"E79")}),-1.0]])]});
            var Q1;
            Q1=makeQuery(id+"F16.imprint","IMPRINT",FACE,{"disambiguationData":[TD([[makeQuery(id+"F16.imprint","IMPRINT",EDGE,{"derivedFrom":sQuery(id+"F16.wireOp",EDGE,"E86")}),-1.0]])]});
            var Q2;
            Q2=makeQuery(id+"F0.imprint","IMPRINT",FACE,{"disambiguationData":[TD([[makeQuery(id+"F0.imprint","IMPRINT",EDGE,{"derivedFrom":sQuery(id+"F0.wireOp",EDGE,"E1.bottom")}),1.0]])]});
            var Q3;
            Q3=makeQuery(id+"F2.opExtrude","CAP_FACE",FACE,{"disambiguationData":[OSD([sQuery(id+"F0.wireOp",EDGE,"E12"),sQuery(id+"F0.wireOp",EDGE,"E13"),sQuery(id+"F0.wireOp",EDGE,"E14"),sQuery(id+"F0.wireOp",EDGE,"E15"),sQuery(id+"F0.wireOp",EDGE,"E17.filletArc"),sQuery(id+"F0.wireOp",EDGE,"E18.filletArc"),sQuery(id+"F0.wireOp",EDGE,"E19.filletArc"),sQuery(id+"F0.wireOp",EDGE,"E20.filletArc"),sQuery(id+"F0.wireOp",EDGE,"E25.0"),sQuery(id+"F0.wireOp",EDGE,"E25.1"),sQuery(id+"F0.wireOp",EDGE,"E25.2"),sQuery(id+"F0.wireOp",EDGE,"E25.3"),sQuery(id+"F0.wireOp",EDGE,"E25.4"),sQuery(id+"F0.wireOp",EDGE,"E25.5"),sQuery(id+"F0.wireOp",EDGE,"E25.6"),sQuery(id+"F0.wireOp",EDGE,"E25.7")])],"isStart":false});
            extrude(context, id + "F18", {"entities" : qUnion([Q0, Q1, Q2]), "endBound" : BoundingType.UP_TO_SURFACE, "depth" : 25 * mm, "endBoundEntityFace" : qUnion([Q3]), "offsetDistance" : 25 * mm});
        }
    });
